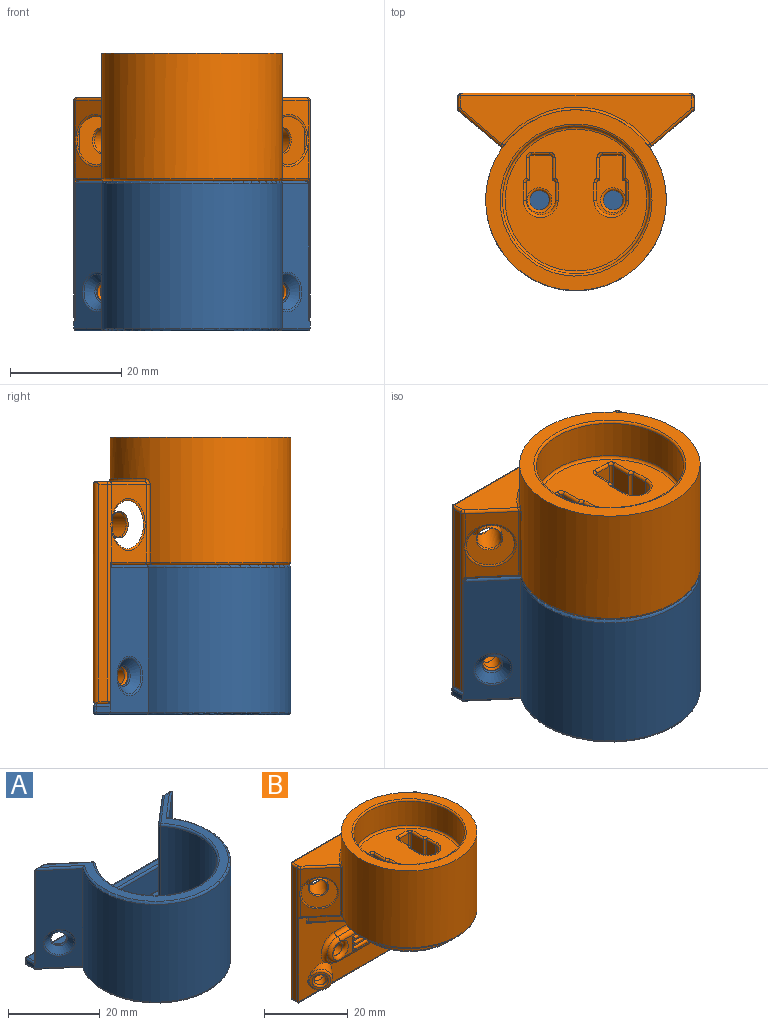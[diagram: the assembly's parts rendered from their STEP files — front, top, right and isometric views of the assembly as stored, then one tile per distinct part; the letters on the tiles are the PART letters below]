
ASSEMBLY  parts=2 mates=1
PART A: 101 faces, bbox 42.8x37.1x27.3 mm
  f0: plane 24.8x8.47mm, normal (-0.65,0.76,0), area 230.5mm2, adj f6,f11,f16,f17,f19,f20,f21,f51
  f1: plane 24.8x8.47mm, normal (0.65,0.76,0), area 230.5mm2, adj f5,f12,f16,f17,f18,f20,f21,f51
  f2: plane 7.13x0.58mm, normal (-0.65,-0.76,0), area 3.6mm2, adj f14,f53,f54,f72
  f3: cylinder r=13.25mm len=26.5mm, axis (0,0,1), area 1450.7mm2, adj f66,f67,f69,f72
  f4: plane 26.08x8.08mm, normal (-0.65,-0.76,0), area 227mm2, adj f8,f22,f58,f60,f77,f84,f97
  f5: plane 24.56x2.81mm, normal (0,1,0), area 68.8mm2, adj f1,f21,f62,f77,f97
  f6: plane 24.56x2.81mm, normal (0,1,0), area 68.8mm2, adj f0,f21,f63,f86,f99
  f7: plane 26.08x8.08mm, normal (0.65,-0.76,0), area 227mm2, adj f8,f28,f56,f61,f86,f87,f99
  f8: cylinder r=16.25mm len=32.5mm, axis (0,0,1), area 1849mm2, adj f4,f7,f59,f85
  f9: plane 39.79x31.5mm, normal (0,0,1), area 152.6mm2, adj f59,f60,f61,f62,f63,f64,f65,f66
  f10: cone r=1.7mm half-angle=45deg, axis (0.65,-0.76,0), area 30.7mm2, adj f55,f56
  f11: cylinder r=1.7mm len=3.4mm, axis (0.65,-0.76,0), area 1.4mm2, adj f0,f55
  f12: cylinder r=1.7mm len=3.4mm, axis (-0.65,-0.76,0), area 1.4mm2, adj f1,f57
  f13: cone r=1.7mm half-angle=45deg, axis (-0.65,-0.76,0), area 30.7mm2, adj f57,f58
  f14: plane 19.39x6mm, normal (0,-1,0), area 116.4mm2, adj f2,f15,f53,f54
  f15: plane 7.13x0.58mm, normal (0.65,-0.76,0), area 3.6mm2, adj f14,f53,f54,f69
  f16: plane 23.49x1.25mm, normal (0,0,1), area 27.5mm2, adj f0,f1,f52,f54
  f17: plane 23.49x1.25mm, normal (0,0,-1), area 27.5mm2, adj f0,f1,f51,f53
  f18: cylinder r=3.5mm len=2.17mm, axis (0,1,0), area 0mm2, adj f1,f20
  f19: cylinder r=3.5mm len=2.17mm, axis (0,1,0), area 0mm2, adj f0,f20
  f20: plane 25x6mm, normal (0,1,0), area 118.4mm2, adj f0,f1,f18,f19,f42,f43,f44,f45
  f21: plane 41.69x31.69mm, normal (0,0,1), area 714.8mm2, adj f0,f1,f5,f6,f30,f31,f34,f35
  f22: plane 2.5x1mm, normal (-1,0,0), area 2.5mm2, adj f4,f77,f81,f83
  f23: plane 16.75x1mm, normal (0,1,0), area 16.8mm2, adj f75,f76,f80,f81
  f24: plane 6x1mm, normal (1,0,0), area 6mm2, adj f35,f39,f41,f75
  f25: plane 6x1mm, normal (0,1,0), area 6mm2, adj f33,f34,f38,f39
  f26: plane 6x1mm, normal (-1,0,0), area 6mm2, adj f30,f32,f33,f95
  f27: plane 16.75x1mm, normal (0,1,0), area 16.8mm2, adj f90,f91,f94,f95
  f28: plane 2.5x1mm, normal (1,0,0), area 2.5mm2, adj f7,f86,f89,f90
  f29: plane 41.5x34.5mm, normal (0,0,-1), area 941mm2, adj f32,f36,f38,f40,f41,f80,f83,f84
  f30: cylinder r=0.5mm len=6mm, axis (0,1,0), area 4.7mm2, adj f21,f26,f31,f93
  f31: torus R=1mm, axis (0,0,-1), area 0.8mm2, adj f21,f30,f33,f34
  f32: cylinder r=0.5mm len=6mm, axis (0,-1,0), area 4.7mm2, adj f26,f29,f36,f96
  f33: cylinder r=0.5mm len=1mm, axis (0,0,-1), area 0.8mm2, adj f25,f26,f31,f36
  f34: cylinder r=0.5mm len=6mm, axis (1,0,0), area 4.7mm2, adj f21,f25,f31,f37
  f35: cylinder r=0.5mm len=6mm, axis (0,-1,0), area 4.7mm2, adj f21,f24,f37,f74
  f36: torus R=1mm, axis (0,0,-1), area 0.8mm2, adj f29,f32,f33,f38
  f37: torus R=1mm, axis (0,0,-1), area 0.8mm2, adj f21,f34,f35,f39
  f38: cylinder r=0.5mm len=6mm, axis (-1,0,0), area 4.7mm2, adj f25,f29,f36,f40
  f39: cylinder r=0.5mm len=1mm, axis (0,0,-1), area 0.8mm2, adj f24,f25,f37,f40
  f40: torus R=1mm, axis (0,0,-1), area 0.8mm2, adj f29,f38,f39,f41
  f41: cylinder r=0.5mm len=6mm, axis (0,1,0), area 4.7mm2, adj f24,f29,f40,f78
  f42: cylinder r=0.5mm len=1mm, axis (0,0,1), area 0.4mm2, adj f20,f43
  f43: cylinder r=0.5mm len=10mm, axis (-1,0,0), area 14.9mm2, adj f20,f42,f44
  f44: cylinder r=0.5mm len=1mm, axis (0,0,-1), area 0.4mm2, adj f20,f43
  f45: cylinder r=0.5mm len=10mm, axis (-1,0,0), area 14.9mm2, adj f20,f46,f47
  f46: cylinder r=0.5mm len=1mm, axis (0,0,-1), area 0.4mm2, adj f20,f45
  f47: cylinder r=0.5mm len=1mm, axis (0,0,1), area 0.4mm2, adj f20,f45
  f48: cylinder r=0.5mm len=1mm, axis (0,0,1), area 0.4mm2, adj f20,f49
  f49: cylinder r=0.5mm len=10mm, axis (-1,0,0), area 14.9mm2, adj f20,f48,f50
  f50: cylinder r=0.5mm len=1mm, axis (0,0,-1), area 0.4mm2, adj f20,f49
  f51: cylinder r=0.5mm len=24.66mm, axis (1,0,0), area 18.9mm2, adj f0,f1,f17,f20
  f52: cylinder r=0.5mm len=24.66mm, axis (-1,0,0), area 18.9mm2, adj f0,f1,f16,f20
  f53: cylinder r=0.5mm len=20.56mm, axis (-1,0,0), area 15.6mm2, adj f0,f1,f2,f14,f15,f17
  f54: cylinder r=0.5mm len=20.56mm, axis (1,0,0), area 15.6mm2, adj f0,f1,f2,f14,f15,f16
  f55: torus R=2.2mm, axis (-0.65,0.76,0), area 4.3mm2, adj f10,f11
  f56: torus R=3.57mm, axis (-0.65,0.76,0), area 8.3mm2, adj f7,f10
  f57: torus R=2.2mm, axis (0.65,0.76,0), area 4.3mm2, adj f12,f13
  f58: torus R=3.57mm, axis (-0.65,-0.76,0), area 8.3mm2, adj f4,f13
  f59: torus R=15.75mm, axis (0,0,1), area 55.6mm2, adj f8,f9,f60,f61
  f60: cylinder r=0.5mm len=8.47mm, axis (0.76,-0.65,0), area 7.8mm2, adj f4,f9,f59,f98
  f61: cylinder r=0.5mm len=8.47mm, axis (0.76,0.65,0), area 7.8mm2, adj f7,f9,f59,f100
  f62: cylinder r=0.5mm len=2.81mm, axis (-1,0,0), area 1.7mm2, adj f5,f9,f64,f98
  f63: cylinder r=0.5mm len=2.81mm, axis (-1,0,0), area 1.7mm2, adj f6,f9,f65,f100
  f64: cylinder r=0.5mm len=8.4mm, axis (-0.76,0.65,0), area 8.3mm2, adj f1,f9,f62,f73
  f65: cylinder r=0.5mm len=8.4mm, axis (-0.76,-0.65,0), area 8.3mm2, adj f0,f9,f63,f70
  f66: torus R=13.75mm, axis (0,0,1), area 48.1mm2, adj f3,f9,f70,f73
  f67: torus R=12.75mm, axis (0,0,-1), area 46.8mm2, adj f3,f21,f68,f71
  f68: bspline ~1.14x1.09mm, area 0.5mm2, adj f0,f21,f67,f69
  f69: cylinder r=0.5mm len=24mm, axis (0,0,1), area 18.9mm2, adj f0,f3,f15,f68,f70
  f70: sphere r=0.5mm, area 0.4mm2, adj f65,f66,f69
  f71: bspline ~1.14x1.09mm, area 0.5mm2, adj f1,f21,f67,f72
  f72: cylinder r=0.5mm len=24mm, axis (0,0,1), area 18.9mm2, adj f1,f2,f3,f71,f73
  f73: sphere r=0.5mm, area 0.4mm2, adj f64,f66,f72
  f74: sphere r=0.5mm, area 0.5mm2, adj f35,f75,f76
  f75: cylinder r=0.5mm len=1mm, axis (0,0,-1), area 0.8mm2, adj f23,f24,f74,f78
  f76: cylinder r=0.5mm len=16.75mm, axis (1,0,0), area 13.2mm2, adj f21,f23,f74,f79
  f77: cylinder r=0.5mm len=2.68mm, axis (0,1,0), area 2mm2, adj f4,f5,f21,f22,f79,f97
  f78: sphere r=0.5mm, area 0.2mm2, adj f41,f75,f80
  f79: sphere r=0.5mm, area 0.5mm2, adj f76,f77,f81
  f80: cylinder r=0.5mm len=16.75mm, axis (-1,0,0), area 13.2mm2, adj f23,f29,f78,f82
  f81: cylinder r=0.5mm len=1mm, axis (0,0,1), area 0.8mm2, adj f22,f23,f79,f82
  f82: sphere r=0.5mm, area 0.5mm2, adj f80,f81,f83
  f83: cylinder r=0.5mm len=2.5mm, axis (0,-1,0), area 1.9mm2, adj f22,f29,f82,f84
  f84: cylinder r=0.5mm len=8.68mm, axis (0.76,-0.65,0), area 8.4mm2, adj f4,f29,f83,f85
  f85: torus R=15.75mm, axis (0,0,-1), area 55.6mm2, adj f8,f29,f84,f87
  f86: cylinder r=0.5mm len=2.68mm, axis (0,-1,0), area 2mm2, adj f6,f7,f21,f28,f88,f99
  f87: cylinder r=0.5mm len=8.68mm, axis (0.76,0.65,0), area 8.4mm2, adj f7,f29,f85,f89
  f88: sphere r=0.5mm, area 0.2mm2, adj f86,f90,f91
  f89: cylinder r=0.5mm len=2.5mm, axis (0,1,0), area 1.9mm2, adj f28,f29,f87,f92
  f90: cylinder r=0.5mm len=1mm, axis (0,0,-1), area 0.8mm2, adj f27,f28,f88,f92
  f91: cylinder r=0.5mm len=16.75mm, axis (1,0,0), area 13.2mm2, adj f21,f27,f88,f93
  f92: sphere r=0.5mm, area 0.2mm2, adj f89,f90,f94
  f93: sphere r=0.5mm, area 0.2mm2, adj f30,f91,f95
  f94: cylinder r=0.5mm len=16.75mm, axis (-1,0,0), area 13.2mm2, adj f27,f29,f92,f96
  f95: cylinder r=0.5mm len=1mm, axis (0,0,-1), area 0.8mm2, adj f26,f27,f93,f96
  f96: sphere r=0.5mm, area 0.4mm2, adj f32,f94,f95
  f97: cylinder r=0.1mm len=24.6mm, axis (0,0,-1), area 6mm2, adj f4,f5,f77,f98
  f98: bspline ~1.35x0.65mm, area 0.1mm2, adj f60,f62,f97
  f99: cylinder r=0.1mm len=24.6mm, axis (0,0,1), area 6mm2, adj f6,f7,f86,f100
  f100: bspline ~1.35x0.54mm, area 0.1mm2, adj f61,f63,f99
PART B: 163 faces, bbox 43.4x40.2x48.5 mm
  f0: cylinder r=1.5mm len=4.54mm, axis (0.65,-0.76,0), area 19.8mm2, adj f152,f154
  f1: cylinder r=3mm len=7.19mm, axis (0.65,-0.76,0), area 41mm2, adj f2,f3,f155
  f2: torus R=4.5mm, axis (0,-1,0), area 18.4mm2, adj f1,f3,f121,f122,f125
  f3: plane 42.63x24.77mm, normal (0,-1,0), area 606.7mm2, adj f1,f2,f5,f83,f85,f88,f90,f92
  f4: cylinder r=1.7mm len=7.27mm, axis (0.65,-0.76,0), area 35.1mm2, adj f152,f161
  f5: cylinder r=3mm len=7.19mm, axis (-0.65,-0.76,0), area 41mm2, adj f3,f124,f158
  f6: cylinder r=1.5mm len=4.52mm, axis (-0.65,-0.76,0), area 19.8mm2, adj f150,f157
  f7: cylinder r=1.7mm len=7.27mm, axis (-0.65,-0.76,0), area 35.1mm2, adj f150,f160
  f8: plane 41.5x8.61mm, normal (0,0,1), area 187.2mm2, adj f40,f41,f42,f44,f46,f47,f114,f116
  f9: plane 15.96x5mm, normal (0,-1,0), area 37.6mm2, adj f98,f99,f100,f101,f102,f103,f104,f105
  f10: cylinder r=2.62mm len=14.5mm, axis (0,0,-1), area 119.6mm2, adj f11,f35,f56,f71
  f11: plane 14.5x3.1mm, normal (1,0,0), area 45mm2, adj f10,f12,f54,f71
  f12: cylinder r=0.5mm len=14.5mm, axis (0,0,-1), area 12mm2, adj f11,f13,f52,f71
  f13: plane 14.5x4mm, normal (1,0,0), area 58mm2, adj f12,f14,f51,f71
  f14: cylinder r=0.5mm len=14.5mm, axis (0,0,-1), area 11.4mm2, adj f13,f15,f53,f71
  f15: plane 14.5x3.16mm, normal (0,-1,0), area 45.9mm2, adj f14,f16,f55,f71
  f16: cylinder r=0.5mm len=14.5mm, axis (0,0,-1), area 11.4mm2, adj f15,f17,f57,f71
  f17: plane 14.5x4mm, normal (-1,0,0), area 58mm2, adj f16,f18,f59,f71
  f18: cylinder r=0.5mm len=14.5mm, axis (0,0,-1), area 12mm2, adj f17,f35,f60,f71
  f19: plane 14.5x3.1mm, normal (-1,0,0), area 45mm2, adj f20,f33,f68,f78
  f20: cylinder r=2.62mm len=14.5mm, axis (0,0,-1), area 119.6mm2, adj f19,f21,f66,f78
  f21: plane 14.5x3.1mm, normal (1,0,0), area 45mm2, adj f20,f22,f64,f78
  f22: cylinder r=0.5mm len=14.5mm, axis (0,0,-1), area 12mm2, adj f21,f23,f62,f78
  f23: plane 14.5x4mm, normal (1,0,0), area 58mm2, adj f22,f24,f61,f78
  f24: cylinder r=0.5mm len=14.5mm, axis (0,0,-1), area 11.4mm2, adj f23,f25,f63,f78
  f25: plane 14.5x3.16mm, normal (0,-1,0), area 45.9mm2, adj f24,f26,f65,f78
  f26: cylinder r=0.5mm len=14.5mm, axis (0,0,-1), area 11.4mm2, adj f25,f27,f67,f78
  f27: plane 14.5x4mm, normal (-1,0,0), area 58mm2, adj f26,f33,f69,f78
  f28: plane 14x7.31mm, normal (0.65,-0.76,0), area 65.7mm2, adj f42,f43,f93,f115,f146
  f29: plane 39x1.54mm, normal (1,0,0), area 60mm2, adj f40,f110,f115,f128
  f30: plane 40.5x39mm, normal (0,1,0), area 1431.2mm2, adj f41,f108,f126,f127,f128,f129,f140,f141
  f31: plane 39x1.54mm, normal (-1,0,0), area 60mm2, adj f44,f107,f113,f129
  f32: plane 14x7.31mm, normal (-0.65,-0.76,0), area 65.7mm2, adj f46,f49,f96,f113,f143
  f33: cylinder r=0.5mm len=14.5mm, axis (0,0,-1), area 12mm2, adj f19,f27,f70,f78
  f34: cylinder r=16.25mm len=32.5mm, axis (0,0,-1), area 1820.2mm2, adj f39,f43,f45,f47,f48,f49,f95
  f35: plane 14.5x3.1mm, normal (-1,0,0), area 45mm2, adj f10,f18,f58,f71
  f36: plane 25.5x25.5mm, normal (0,0,1), area 384mm2, adj f50,f51,f52,f53,f54,f55,f56,f57
  f37: plane 39.79x31.5mm, normal (0,0,-1), area 153mm2, adj f86,f89,f91,f93,f94,f95,f96,f97
  f38: cylinder r=13.25mm len=26.5mm, axis (0,0,-1), area 589mm2, adj f50,f162
  f39: plane 32.5x32.5mm, normal (0,0,1), area 242.1mm2, adj f34,f162
  f40: cylinder r=0.5mm len=2.25mm, axis (0,-1,0), area 1.5mm2, adj f8,f29,f41,f116,f128
  f41: cylinder r=0.5mm len=41.91mm, axis (1,0,0), area 32.5mm2, adj f8,f30,f40,f44,f128,f129
  f42: cylinder r=0.5mm len=7.63mm, axis (-0.76,-0.65,0), area 7.5mm2, adj f8,f28,f45,f116
  f43: cylinder r=0.5mm len=14mm, axis (0,0,-1), area 10.2mm2, adj f28,f34,f45,f94
  f44: cylinder r=0.5mm len=2.25mm, axis (0,1,0), area 1.5mm2, adj f8,f31,f41,f114,f129
  f45: bspline ~1.22x1.17mm, area 0.8mm2, adj f34,f42,f43,f47
  f46: cylinder r=0.5mm len=7.63mm, axis (-0.76,0.65,0), area 7.5mm2, adj f8,f32,f48,f114
  f47: torus R=16.75mm, axis (0,0,1), area 23.8mm2, adj f8,f34,f45,f48
  f48: bspline ~1.19x1.17mm, area 0.8mm2, adj f34,f46,f47,f49
  f49: cylinder r=0.5mm len=14mm, axis (0,0,-1), area 10.2mm2, adj f32,f34,f48,f97
  f50: torus R=12.75mm, axis (0,0,1), area 64.5mm2, adj f36,f38
  f51: cylinder r=0.5mm len=4mm, axis (0,-1,0), area 3mm2, adj f13,f36,f52,f53
  f52: torus R=1mm, axis (0,0,1), area 0.7mm2, adj f12,f36,f51,f54
  f53: torus R=1mm, axis (0,0,1), area 0.8mm2, adj f14,f36,f51,f55
  f54: cylinder r=0.5mm len=3.1mm, axis (0,-1,0), area 2.4mm2, adj f11,f36,f52,f56
  f55: cylinder r=0.5mm len=3.16mm, axis (-1,0,0), area 2.5mm2, adj f15,f36,f53,f57
  f56: torus R=3.12mm, axis (0,0,1), area 6.9mm2, adj f10,f36,f54,f58
  f57: torus R=1mm, axis (0,0,1), area 0.8mm2, adj f16,f36,f55,f59
  f58: cylinder r=0.5mm len=3.1mm, axis (0,1,0), area 2.4mm2, adj f35,f36,f56,f60
  f59: cylinder r=0.5mm len=4mm, axis (0,1,0), area 3mm2, adj f17,f36,f57,f60
  f60: torus R=1mm, axis (0,0,1), area 0.7mm2, adj f18,f36,f58,f59
  f61: cylinder r=0.5mm len=4mm, axis (0,-1,0), area 3mm2, adj f23,f36,f62,f63
  f62: torus R=1mm, axis (0,0,1), area 0.7mm2, adj f22,f36,f61,f64
  f63: torus R=1mm, axis (0,0,1), area 0.8mm2, adj f24,f36,f61,f65
  f64: cylinder r=0.5mm len=3.1mm, axis (0,-1,0), area 2.4mm2, adj f21,f36,f62,f66
  f65: cylinder r=0.5mm len=3.16mm, axis (-1,0,0), area 2.5mm2, adj f25,f36,f63,f67
  f66: torus R=3.12mm, axis (0,0,1), area 6.9mm2, adj f20,f36,f64,f68
  f67: torus R=1mm, axis (0,0,1), area 0.8mm2, adj f26,f36,f65,f69
  f68: cylinder r=0.5mm len=3.1mm, axis (0,1,0), area 2.4mm2, adj f19,f36,f66,f70
  f69: cylinder r=0.5mm len=4mm, axis (0,1,0), area 3mm2, adj f27,f36,f67,f70
  f70: torus R=1mm, axis (0,0,1), area 0.7mm2, adj f33,f36,f68,f69
  f71: plane 10.73x5.25mm, normal (0,0,1), area 32.3mm2, adj f10,f11,f12,f13,f14,f15,f16,f17
  f72: cylinder r=13.25mm len=26.5mm, axis (0,0,1), area 122.9mm2, adj f73,f75,f84,f89
  f73: plane 8.32x7.12mm, normal (0.65,-0.76,0), area 21.9mm2, adj f72,f82,f83,f86
  f74: cylinder r=1.75mm len=3.5mm, axis (0,0,1), area 22mm2, adj f111,f148
  f75: plane 8.32x7.12mm, normal (-0.65,-0.76,0), area 21.9mm2, adj f72,f87,f91,f92
  f76: cylinder r=1.75mm len=3.5mm, axis (0,0,1), area 22mm2, adj f112,f149
  f77: plane 33.64x28.5mm, normal (0,0,-1), area 606mm2, adj f82,f84,f87,f88,f111,f112
  f78: plane 10.73x5.25mm, normal (0,0,1), area 32.3mm2, adj f19,f20,f21,f22,f23,f24,f25,f26
  f79: plane 41.5x2mm, normal (0,0,-1), area 83mm2, adj f107,f108,f109,f110
  f80: cylinder r=1.7mm len=3.4mm, axis (0,-1,0), area 32mm2, adj f118,f127
  f81: cylinder r=1.7mm len=3.4mm, axis (0,-1,0), area 32mm2, adj f119,f126
  f82: cylinder r=0.5mm len=9.05mm, axis (-0.76,-0.65,0), area 8.3mm2, adj f73,f77,f84,f85
  f83: cylinder r=0.5mm len=2mm, axis (0,0,1), area 0.7mm2, adj f3,f73,f85,f136
  f84: torus R=12.75mm, axis (0,0,1), area 48mm2, adj f72,f77,f82,f87
  f85: bspline ~1.61x1.04mm, area 0.9mm2, adj f3,f82,f83,f88
  f86: cylinder r=0.5mm len=8.65mm, axis (0.76,0.65,0), area 8.4mm2, adj f37,f73,f89,f136
  f87: cylinder r=0.5mm len=9.05mm, axis (-0.76,0.65,0), area 8.3mm2, adj f75,f77,f84,f90
  f88: cylinder r=0.5mm len=33.64mm, axis (1,0,0), area 26.4mm2, adj f3,f77,f85,f90
  f89: torus R=13.75mm, axis (0,0,1), area 48.5mm2, adj f37,f72,f86,f91
  f90: bspline ~1.61x1mm, area 0.9mm2, adj f3,f87,f88,f92
  f91: cylinder r=0.5mm len=8.65mm, axis (0.76,-0.65,0), area 8.4mm2, adj f37,f75,f89,f139
  f92: cylinder r=0.5mm len=2mm, axis (0,0,1), area 0.7mm2, adj f3,f75,f90,f139
  f93: cylinder r=0.5mm len=7.8mm, axis (0.76,0.65,0), area 7.4mm2, adj f28,f37,f94,f115,f134
  f94: torus R=1mm, axis (0,0,1), area 0.8mm2, adj f37,f43,f93,f95
  f95: torus R=15.75mm, axis (0,0,1), area 54.5mm2, adj f34,f37,f94,f97
  f96: cylinder r=0.5mm len=7.8mm, axis (0.76,-0.65,0), area 7.4mm2, adj f32,f37,f97,f113,f137
  f97: torus R=1mm, axis (0,0,1), area 0.8mm2, adj f37,f49,f95,f96
  f98: cylinder r=0.5mm len=1mm, axis (0,0,-1), area 0.4mm2, adj f9,f99
  f99: cylinder r=0.5mm len=10mm, axis (1,0,0), area 14.9mm2, adj f9,f98,f100
  f100: cylinder r=0.5mm len=1mm, axis (0,0,1), area 0.4mm2, adj f9,f99
  f101: cylinder r=0.5mm len=1mm, axis (0,0,1), area 0.4mm2, adj f9,f102
  f102: cylinder r=0.5mm len=10mm, axis (1,0,0), area 14.9mm2, adj f9,f101,f103
  f103: cylinder r=0.5mm len=1mm, axis (0,0,-1), area 0.4mm2, adj f9,f102
  f104: cylinder r=0.5mm len=1mm, axis (0,0,-1), area 0.4mm2, adj f9,f105
  f105: cylinder r=0.5mm len=10mm, axis (1,0,0), area 14.9mm2, adj f9,f104,f106
  f106: cylinder r=0.5mm len=1mm, axis (0,0,1), area 0.4mm2, adj f9,f105
  f107: cylinder r=0.5mm len=2.63mm, axis (0,-1,0), area 1.7mm2, adj f31,f79,f108,f109,f113,f129
  f108: cylinder r=0.5mm len=41.91mm, axis (-1,0,0), area 32.5mm2, adj f30,f79,f107,f110,f128,f129
  f109: cylinder r=0.5mm len=42.35mm, axis (-1,0,0), area 33mm2, adj f3,f79,f107,f110,f113,f115
  f110: cylinder r=0.5mm len=2.63mm, axis (0,1,0), area 1.7mm2, adj f29,f79,f108,f109,f115,f128
  f111: torus R=2.25mm, axis (0,0,1), area 9.5mm2, adj f74,f77
  f112: torus R=2.25mm, axis (0,0,1), area 9.5mm2, adj f76,f77
  f113: cylinder r=1mm len=39.27mm, axis (0,0,1), area 24mm2, adj f3,f31,f32,f96,f107,f109,f114,f137
  f114: torus R=0.5mm, axis (0,0,1), area 0.6mm2, adj f8,f44,f46,f113
  f115: cylinder r=1mm len=39.27mm, axis (0,0,-1), area 24mm2, adj f3,f28,f29,f93,f109,f110,f116,f134
  f116: torus R=0.5mm, axis (0,0,1), area 0.6mm2, adj f8,f40,f42,f115
  f117: cylinder r=1mm len=18mm, axis (-1,0,0), area 28.2mm2, adj f9,f118,f119,f120,f121,f122
  f118: torus R=2.7mm, axis (0,-1,0), area 19.4mm2, adj f9,f80,f117,f122,f123
  f119: torus R=2.7mm, axis (0,-1,0), area 19.4mm2, adj f9,f81,f117,f120,f123
  f120: torus R=2.5mm, axis (0,-1,0), area 14.7mm2, adj f117,f119,f123,f124
  f121: cylinder r=1mm len=18mm, axis (1,0,0), area 28.3mm2, adj f2,f3,f117,f124
  f122: torus R=2.5mm, axis (0,-1,0), area 14.7mm2, adj f2,f117,f118,f123
  f123: cylinder r=1mm len=18mm, axis (1,0,0), area 28.2mm2, adj f9,f118,f119,f120,f122,f125
  f124: torus R=4.5mm, axis (0,-1,0), area 18.4mm2, adj f3,f5,f120,f121,f125
  f125: cylinder r=1mm len=18mm, axis (-1,0,0), area 28.3mm2, adj f2,f3,f123,f124
  f126: torus R=2.7mm, axis (0,1,0), area 20.4mm2, adj f30,f81
  f127: torus R=2.7mm, axis (0,1,0), area 20.4mm2, adj f30,f80
  f128: cylinder r=1mm len=39.91mm, axis (0,0,-1), area 62mm2, adj f29,f30,f40,f41,f108,f110
  f129: cylinder r=1mm len=39.91mm, axis (0,0,-1), area 62mm2, adj f30,f31,f41,f44,f107,f108
  f130: cone r=2.25mm half-angle=45deg, axis (-0.65,-0.76,0), area 57.9mm2, adj f142,f143,f144
  f131: cylinder r=2.25mm len=8.67mm, axis (-0.65,-0.76,0), area 73.1mm2, adj f141,f142
  f132: cylinder r=2.25mm len=8.67mm, axis (0.65,-0.76,0), area 73.1mm2, adj f140,f145
  f133: cone r=2.25mm half-angle=45deg, axis (0.65,-0.76,0), area 57.9mm2, adj f145,f146,f147
  f134: bspline ~1.75x1.54mm, area 0.8mm2, adj f3,f93,f115,f135
  f135: cylinder r=0.5mm len=1.54mm, axis (1,0,0), area 1.2mm2, adj f3,f37,f134,f136
  f136: sphere r=0.5mm, area 0.2mm2, adj f83,f86,f135
  f137: bspline ~1.46x0.85mm, area 0.8mm2, adj f3,f96,f113,f138
  f138: cylinder r=0.5mm len=1.54mm, axis (1,0,0), area 1.2mm2, adj f3,f37,f137,f139
  f139: sphere r=0.5mm, area 0.3mm2, adj f91,f92,f138
  f140: bspline ~7.23x5.5mm, area 14.2mm2, adj f30,f132
  f141: bspline ~7.23x5.5mm, area 14.2mm2, adj f30,f131
  f142: torus R=2.75mm, axis (0.65,0.76,0), area 5.7mm2, adj f130,f131
  f143: torus R=4.69mm, axis (0.65,0.76,0), area 10.4mm2, adj f32,f130,f144
  f144: bspline ~2.24x0.51mm, area 0.8mm2, adj f113,f130,f143
  f145: torus R=2.75mm, axis (-0.65,0.76,0), area 5.7mm2, adj f132,f133
  f146: torus R=4.69mm, axis (0.65,-0.76,0), area 10.4mm2, adj f28,f133,f147
  f147: bspline ~2.24x0.51mm, area 0.8mm2, adj f115,f133,f146
  f148: torus R=2.25mm, axis (0,0,1), area 9.5mm2, adj f74,f78
  f149: torus R=2.25mm, axis (0,0,1), area 9.5mm2, adj f71,f76
  f150: plane 5.01x3.94mm, normal (0,1,0), area 2.6mm2, adj f6,f7
  f151: plane 5x4.03mm, normal (-0.65,-0.76,0), area 7.5mm2, adj f157,f158,f159
  f152: plane 4.47x3.4mm, normal (0,1,0), area 2.6mm2, adj f0,f4
  f153: plane 5x4.03mm, normal (0.65,-0.76,0), area 7.5mm2, adj f154,f155,f156
  f154: torus R=2mm, axis (0.65,-0.76,0), area 8.3mm2, adj f0,f153
  f155: torus R=2.5mm, axis (0.65,-0.76,0), area 11.2mm2, adj f1,f153,f156
  f156: bspline ~3.96x0.94mm, area 1.5mm2, adj f3,f153,f155
  f157: torus R=2mm, axis (-0.65,-0.76,0), area 8.3mm2, adj f6,f151
  f158: torus R=2.5mm, axis (-0.65,-0.76,0), area 11.2mm2, adj f5,f151,f159
  f159: bspline ~3.96x0.94mm, area 1.5mm2, adj f3,f151,f158
  f160: bspline ~5.79x4.4mm, area 11.1mm2, adj f7,f30
  f161: bspline ~5.79x4.4mm, area 11.1mm2, adj f4,f30
  f162: torus R=13.67mm, axis (0,0,1), area 56.2mm2, adj f38,f39
PLACE A t=(-24.79,13.66,84.75)mm
PLACE B t=(-24.79,13.66,84.75)mm
MATE fastened B.f34 <-> A.f3  axis (0,0,-1) through (-24.79,13.66,84.75)mm
